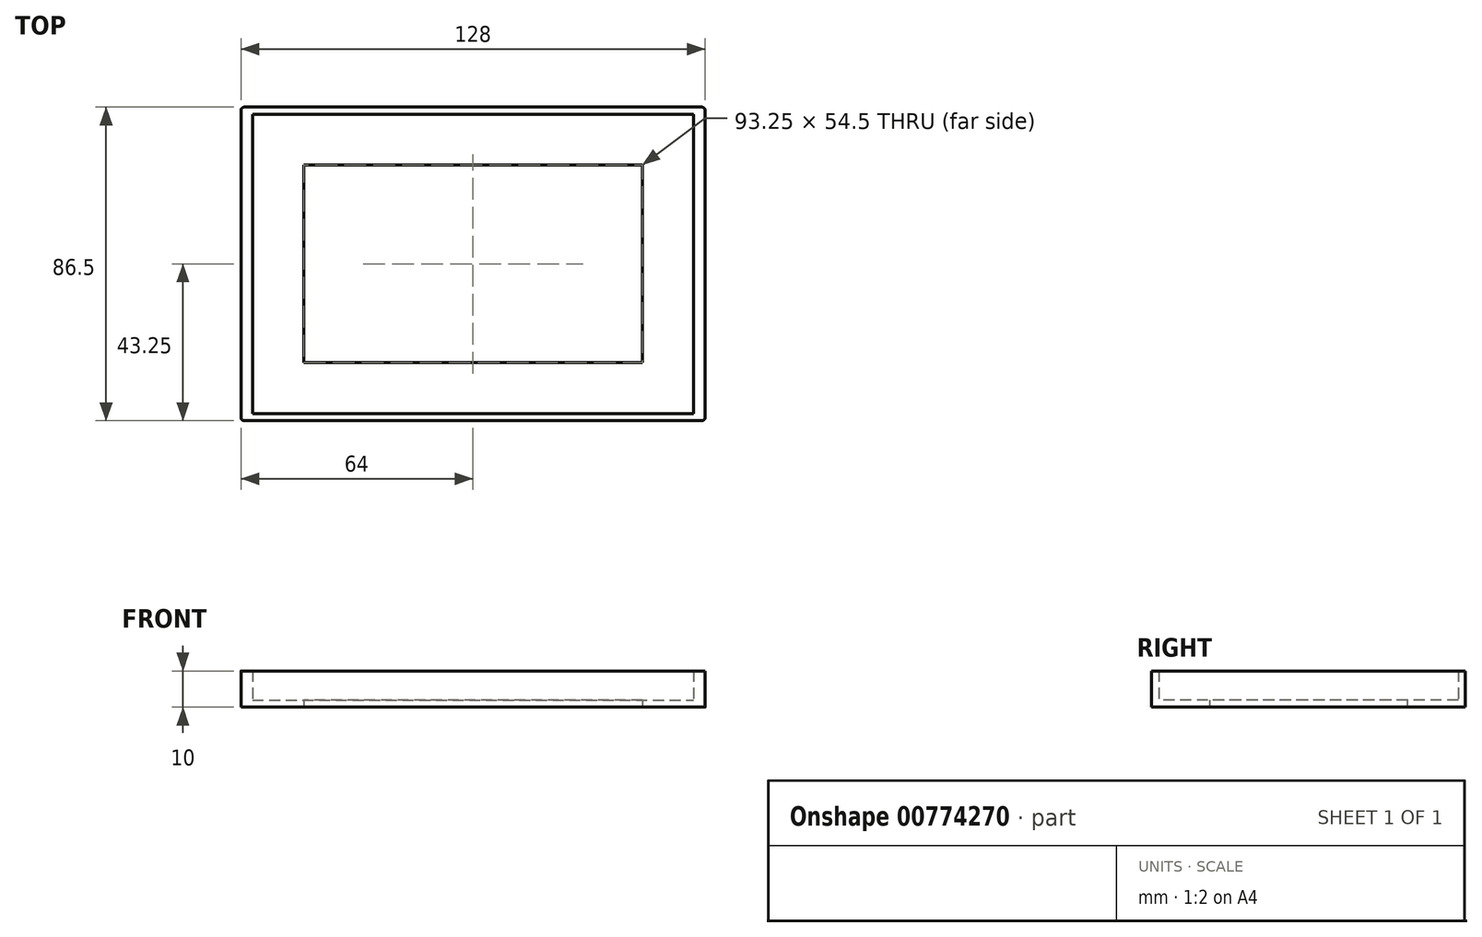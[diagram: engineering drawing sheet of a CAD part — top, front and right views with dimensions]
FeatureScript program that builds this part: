
annotation { "Feature Type Name" : "Feature", "Feature Type Description" : "" }
export const myFeature = defineFeature(function(context is Context, id is Id, definition is map)
    precondition{}
    {
        {
            var Q0;
            Q0=qCreatedBy(makeId("Top.planeOp"),FACE);
            var sketch = newSketch(context, id + "F0", { "sketchPlane" : qUnion([Q0])});
            skLineSegment(sketch, "E0.bottom", {"start": v(64, -43.25) * mm, "end": v(-64, -43.25) * mm});
            skLineSegment(sketch, "E0.top", {"start": v(64, 43.25) * mm, "end": v(-64, 43.25) * mm});
            skLineSegment(sketch, "E0.left", {"start": v(64, -43.25) * mm, "end": v(64, 43.25) * mm});
            skLineSegment(sketch, "E0.right", {"start": v(-64, -43.25) * mm, "end": v(-64, 43.25) * mm});
            skPoint(sketch, "E0.middle", {"position": v(0, 0) * mm});
            skLineSegment(sketch, "E1.bottom", {"start": v(46.63, 27.25) * mm, "end": v(-46.62, 27.25) * mm});
            skLineSegment(sketch, "E1.top", {"start": v(46.63, -27.25) * mm, "end": v(-46.62, -27.25) * mm});
            skLineSegment(sketch, "E1.left", {"start": v(46.63, 27.25) * mm, "end": v(46.63, -27.25) * mm});
            skLineSegment(sketch, "E1.right", {"start": v(-46.62, 27.25) * mm, "end": v(-46.62, -27.25) * mm});
            skSolve(sketch);
        }
        {
            var Q0;
            Q0=makeQuery(id+"F0.imprint","IMPRINT",FACE,{"disambiguationData":[TD([[makeQuery(id+"F0.imprint","IMPRINT",EDGE,{"derivedFrom":sQuery(id+"F0.wireOp",EDGE,"E0.bottom")}),-1.0]])]});
            extrude(context, id + "F1", {"entities" : qUnion([Q0]), "depth" : 2 * mm, "offsetDistance" : 25 * mm});
        }
        {
            var Q0;
            Q0=makeQuery(id+"F1.opExtrude","CAP_FACE",FACE,{"disambiguationData":[OSD([sQuery(id+"F0.wireOp",EDGE,"E0.bottom"),sQuery(id+"F0.wireOp",EDGE,"E0.top"),sQuery(id+"F0.wireOp",EDGE,"E0.left"),sQuery(id+"F0.wireOp",EDGE,"E0.right"),sQuery(id+"F0.wireOp",EDGE,"E1.bottom"),sQuery(id+"F0.wireOp",EDGE,"E1.top"),sQuery(id+"F0.wireOp",EDGE,"E1.left"),sQuery(id+"F0.wireOp",EDGE,"E1.right")])],"isStart":false});
            var sketch = newSketch(context, id + "F2", { "sketchPlane" : qUnion([Q0])});
            skLineSegment(sketch, "E2.bottom", {"start": v(64, 43.25) * mm, "end": v(60.8, 43.25) * mm});
            skLineSegment(sketch, "E2.top", {"start": v(64, -43.25) * mm, "end": v(60.8, -43.25) * mm});
            skLineSegment(sketch, "E2.left", {"start": v(64, 43.25) * mm, "end": v(64, -43.25) * mm});
            skLineSegment(sketch, "E2.right", {"start": v(60.8, 43.25) * mm, "end": v(60.8, -43.25) * mm});
            skLineSegment(sketch, "E3.bottom", {"start": v(-64, 43.25) * mm, "end": v(-60.8, 43.25) * mm});
            skLineSegment(sketch, "E3.top", {"start": v(-64, -43.25) * mm, "end": v(-60.8, -43.25) * mm});
            skLineSegment(sketch, "E3.left", {"start": v(-64, 43.25) * mm, "end": v(-64, -43.25) * mm});
            skLineSegment(sketch, "E3.right", {"start": v(-60.8, 43.25) * mm, "end": v(-60.8, -43.25) * mm});
            skLineSegment(sketch, "E4.bottom", {"start": v(-64, -43.25) * mm, "end": v(64, -43.25) * mm});
            skLineSegment(sketch, "E4.top", {"start": v(-64, -41.25) * mm, "end": v(64, -41.25) * mm});
            skLineSegment(sketch, "E4.left", {"start": v(-64, -43.25) * mm, "end": v(-64, -41.25) * mm});
            skLineSegment(sketch, "E4.right", {"start": v(64, -43.25) * mm, "end": v(64, -41.25) * mm});
            skLineSegment(sketch, "E5", {"start": v(46.62, 0) * mm, "end": v(-46.62, 0) * mm});
            skLineSegment(sketch, "E6.MirrorCS", {"start": v(-64, 41.25) * mm, "end": v(64, 41.25) * mm});
            skSolve(sketch);
        }
        {
            var Q0;
            {var subQ0=sQuery(id+"F2.wireOp",EDGE,"E4.top");var subQ1=sQuery(id+"F2.wireOp",EDGE,"E3.left");var subQ2=makeQuery(id+"F2.imprint","INTERSECT",VERTEX,{"derivedFrom":[subQ1,subQ0]});Q0=makeQuery(id+"F2.imprint","IMPRINT",FACE,{"disambiguationData":[TD([[makeQuery(id+"F2.imprint","IMPRINT",EDGE,{"disambiguationData":[TD([[subQ2,-1.0]])],"derivedFrom":subQ1}),-1.0]])]});}
            var Q1;
            {var subQ0=sQuery(id+"F2.wireOp",EDGE,"E3.bottom");Q1=makeQuery(id+"F2.imprint","IMPRINT",FACE,{"disambiguationData":[TD([[makeQuery(id+"F2.imprint","IMPRINT",EDGE,{"derivedFrom":subQ0}),1.0]])]});}
            var Q2;
            {var subQ0=sQuery(id+"F2.wireOp",EDGE,"E2.right");var subQ3=sQuery(id+"F2.wireOp",EDGE,"E6.MirrorCS");var subQ4=makeQuery(id+"F2.imprint","INTERSECT",VERTEX,{"derivedFrom":[subQ0,subQ3]});Q2=makeQuery(id+"F2.imprint","IMPRINT",FACE,{"disambiguationData":[TD([[makeQuery(id+"F2.imprint","IMPRINT",EDGE,{"disambiguationData":[TD([[subQ4,1.0]])],"derivedFrom":subQ3}),1.0]])]});}
            var Q3;
            {var subQ0=sQuery(id+"F2.wireOp",EDGE,"E2.bottom");Q3=makeQuery(id+"F2.imprint","IMPRINT",FACE,{"disambiguationData":[TD([[makeQuery(id+"F2.imprint","IMPRINT",EDGE,{"derivedFrom":subQ0}),1.0]])]});}
            var Q4;
            {var subQ0=sQuery(id+"F2.wireOp",EDGE,"E4.top");var subQ1=sQuery(id+"F2.wireOp",EDGE,"E2.left");var subQ2=makeQuery(id+"F2.imprint","INTERSECT",VERTEX,{"derivedFrom":[subQ1,subQ0]});Q4=makeQuery(id+"F2.imprint","IMPRINT",FACE,{"disambiguationData":[TD([[makeQuery(id+"F2.imprint","IMPRINT",EDGE,{"disambiguationData":[TD([[subQ2,-1.0]])],"derivedFrom":subQ1}),1.0]])]});}
            var Q5;
            {var subQ0=sQuery(id+"F2.wireOp",EDGE,"E2.top");Q5=makeQuery(id+"F2.imprint","IMPRINT",FACE,{"disambiguationData":[TD([[makeQuery(id+"F2.imprint","IMPRINT",EDGE,{"derivedFrom":subQ0}),-1.0]])]});}
            var Q6;
            {var subQ0=sQuery(id+"F2.wireOp",EDGE,"E4.bottom");Q6=makeQuery(id+"F2.imprint","IMPRINT",FACE,{"disambiguationData":[TD([[makeQuery(id+"F2.imprint","IMPRINT",EDGE,{"derivedFrom":subQ0}),-1.0]])]});}
            var Q7;
            {var subQ0=sQuery(id+"F2.wireOp",EDGE,"E3.top");Q7=makeQuery(id+"F2.imprint","IMPRINT",FACE,{"disambiguationData":[TD([[makeQuery(id+"F2.imprint","IMPRINT",EDGE,{"derivedFrom":subQ0}),-1.0]])]});}
            var Q8;
            Q8=sQuery(id+"F2.wireOp",EDGE,"E3.right");
            var Q9;
            Q9=sQuery(id+"F2.wireOp",EDGE,"E6.MirrorCS");
            var Q10;
            Q10=sQuery(id+"F2.wireOp",EDGE,"E3.left");
            var Q11;
            Q11=sQuery(id+"F2.wireOp",EDGE,"E3.bottom");
            var Q12;
            Q12=sQuery(id+"F2.wireOp",EDGE,"E3.top");
            var Q13;
            Q13=sQuery(id+"F2.wireOp",EDGE,"E4.top");
            var Q14;
            Q14=sQuery(id+"F2.wireOp",EDGE,"E4.bottom");
            var Q15;
            Q15=sQuery(id+"F2.wireOp",EDGE,"E2.right");
            var Q16;
            Q16=sQuery(id+"F2.wireOp",EDGE,"E2.left");
            extrude(context, id + "F3", {"entities" : qUnion([Q0, Q1, Q2, Q3, Q4, Q5, Q6, Q7]), "operationType" : NewBodyOperationType.ADD, "surfaceEntities" : qUnion([Q8, Q9, Q10, Q11, Q12, Q13, Q14, Q15, Q16]), "depth" : 8 * mm, "offsetDistance" : 25 * mm});
        }
        {
            var Q0;
            Q0=makeQuery(id+"F3.boolean.opBoolean","MERGE",EDGE,{"derivedFrom":[makeQuery(id+"F1.opExtrude","SWEPT_EDGE",EDGE,{"disambiguationData":[OSD([sQuery(id+"F0.wireOp",EDGE,"E0.bottom"),sQuery(id+"F0.wireOp",EDGE,"E0.right")])]}),makeQuery(id+"F3.opExtrude","SWEPT_EDGE",EDGE,{"disambiguationData":[OSD([sQuery(id+"F2.wireOp",EDGE,"E3.top"),sQuery(id+"F2.wireOp",EDGE,"E3.left")])]})]});
            var Q1;
            Q1=makeQuery(id+"F3.boolean.opBoolean","MERGE",EDGE,{"derivedFrom":[makeQuery(id+"F1.opExtrude","SWEPT_EDGE",EDGE,{"disambiguationData":[OSD([sQuery(id+"F0.wireOp",EDGE,"E0.top"),sQuery(id+"F0.wireOp",EDGE,"E0.right")])]}),makeQuery(id+"F3.opExtrude","SWEPT_EDGE",EDGE,{"disambiguationData":[OSD([sQuery(id+"F2.wireOp",EDGE,"E3.bottom"),sQuery(id+"F2.wireOp",EDGE,"E3.left")])]})]});
            var Q2;
            Q2=makeQuery(id+"F3.boolean.opBoolean","MERGE",EDGE,{"derivedFrom":[makeQuery(id+"F1.opExtrude","SWEPT_EDGE",EDGE,{"disambiguationData":[OSD([sQuery(id+"F0.wireOp",EDGE,"E0.bottom"),sQuery(id+"F0.wireOp",EDGE,"E0.left")])]}),makeQuery(id+"F3.opExtrude","SWEPT_EDGE",EDGE,{"disambiguationData":[OSD([sQuery(id+"F2.wireOp",EDGE,"E2.top"),sQuery(id+"F2.wireOp",EDGE,"E2.left")])]})]});
            var Q3;
            Q3=makeQuery(id+"F3.boolean.opBoolean","MERGE",EDGE,{"derivedFrom":[makeQuery(id+"F1.opExtrude","SWEPT_EDGE",EDGE,{"disambiguationData":[OSD([sQuery(id+"F0.wireOp",EDGE,"E0.top"),sQuery(id+"F0.wireOp",EDGE,"E0.left")])]}),makeQuery(id+"F3.opExtrude","SWEPT_EDGE",EDGE,{"disambiguationData":[OSD([sQuery(id+"F2.wireOp",EDGE,"E2.bottom"),sQuery(id+"F2.wireOp",EDGE,"E2.left")])]})]});
            fillet(context, id + "F4", {"entities" : qUnion([Q0, Q1, Q2, Q3]), "tangentPropagation" : true, "radius" : 1 * mm, "defaultsChanged" : false, "vertexSettings" : [], "allowEdgeOverflow" : false});
        }
    });
